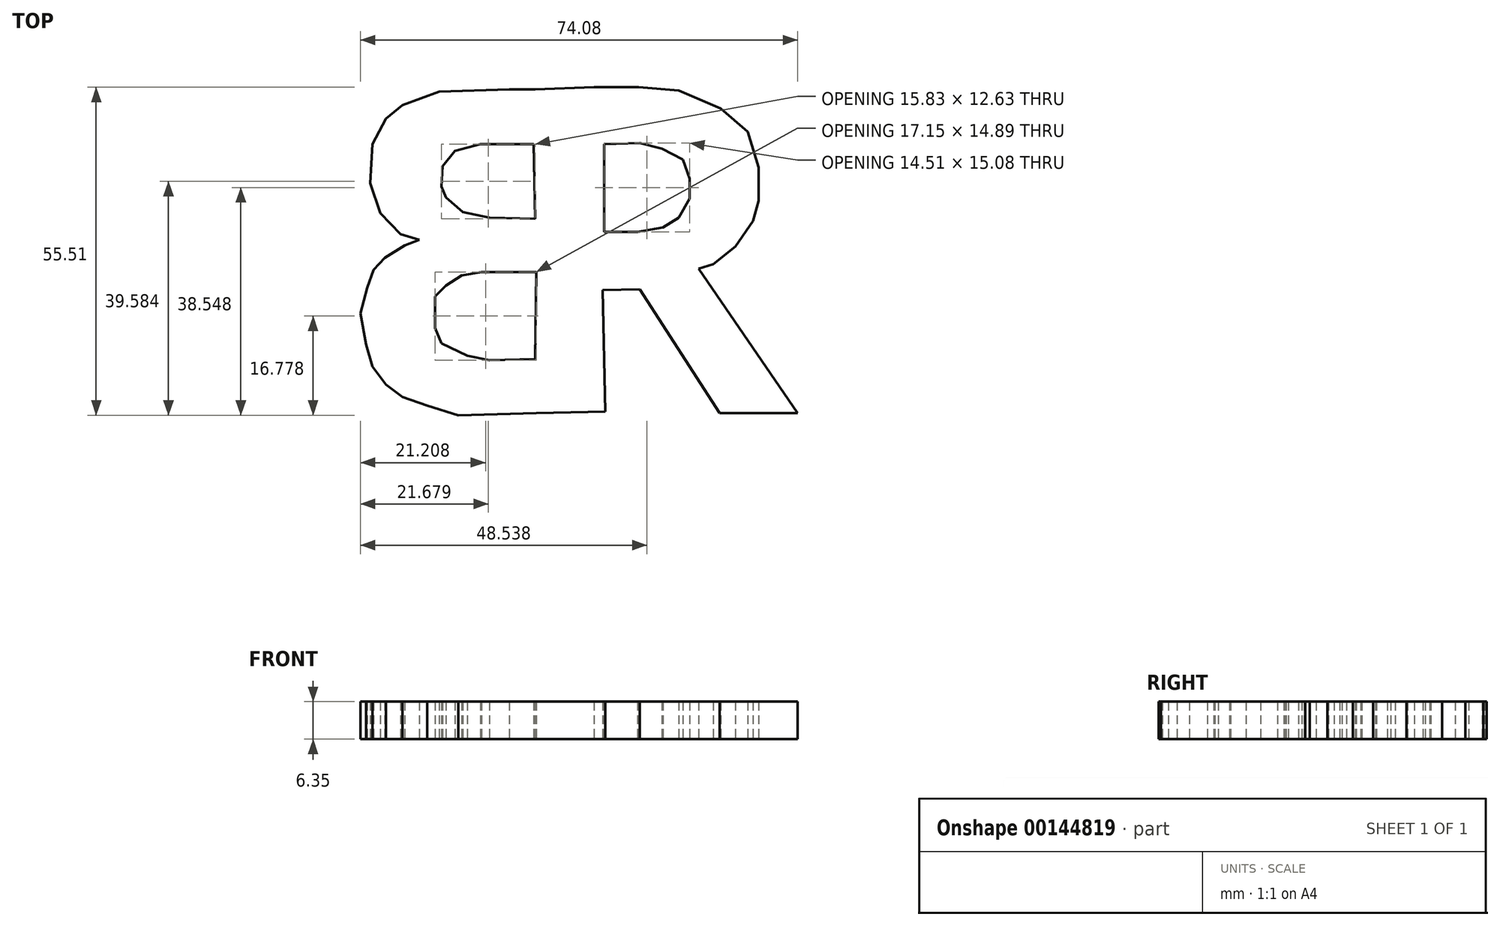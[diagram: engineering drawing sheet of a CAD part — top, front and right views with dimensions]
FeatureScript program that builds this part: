
annotation { "Feature Type Name" : "Feature", "Feature Type Description" : "" }
export const myFeature = defineFeature(function(context is Context, id is Id, definition is map)
    precondition{}
    {
        {
            var Q0;
            Q0=qCreatedBy(makeId("Top.planeOp"),FACE);
            var sketch = newSketch(context, id + "F0", { "sketchPlane" : qUnion([Q0])});
            skLineSegment(sketch, "E0.MirrorCS", {"start": v(-8.3, 21.58) * mm, "end": v(-10.18, 19.7) * mm});
            skLineSegment(sketch, "E1.MirrorCS", {"start": v(0.38, 45.52) * mm, "end": v(-2.45, 45.52) * mm});
            skLineSegment(sketch, "E2.MirrorCS", {"start": v(-9.05, 11.78) * mm, "end": v(-6.6, 10.84) * mm});
            skLineSegment(sketch, "E3.MirrorCS", {"start": v(-8.86, 41.75) * mm, "end": v(-9.05, 38.36) * mm});
            skLineSegment(sketch, "E4.MirrorCS", {"start": v(-8.3, 36.47) * mm, "end": v(-5.47, 34.02) * mm});
            skLineSegment(sketch, "E5.MirrorCS", {"start": v(-2.45, 45.52) * mm, "end": v(-6.79, 44.39) * mm});
            skLineSegment(sketch, "E6.MirrorCS", {"start": v(-15.64, 52.11) * mm, "end": v(-18.47, 49.85) * mm});
            skLineSegment(sketch, "E7.MirrorCS", {"start": v(-4.71, 9.7) * mm, "end": v(-9.05, 11.78) * mm});
            skLineSegment(sketch, "E8.MirrorCS", {"start": v(-15.27, 28.37) * mm, "end": v(-18.66, 26.3) * mm});
            skLineSegment(sketch, "E9.MirrorCS", {"start": v(-18.66, 26.3) * mm, "end": v(-20.54, 24.22) * mm});
            skLineSegment(sketch, "E10.MirrorCS", {"start": v(-12.82, 29.3) * mm, "end": v(-15.27, 28.37) * mm});
            skLineSegment(sketch, "E11.MirrorCS", {"start": v(-15.64, 2.73) * mm, "end": v(-11.5, 1.23) * mm});
            skLineSegment(sketch, "E12.MirrorCS", {"start": v(-10.18, 19.7) * mm, "end": v(-10.18, 17.06) * mm});
            skLineSegment(sketch, "E13.MirrorCS", {"start": v(-10.18, 14.42) * mm, "end": v(-9.05, 11.78) * mm});
            skLineSegment(sketch, "E14.MirrorCS", {"start": v(-10.18, 17.06) * mm, "end": v(-10.18, 14.42) * mm});
            skLineSegment(sketch, "E15.MirrorCS", {"start": v(-16.02, 30.25) * mm, "end": v(-12.82, 29.3) * mm});
            skLineSegment(sketch, "E16.MirrorCS", {"start": v(-19.41, 33.83) * mm, "end": v(-16.02, 30.25) * mm});
            skLineSegment(sketch, "E17.MirrorCS", {"start": v(-4.71, 9.7) * mm, "end": v(-0.94, 8.95) * mm});
            skLineSegment(sketch, "E18.MirrorCS", {"start": v(-6.79, 44.39) * mm, "end": v(-8.86, 41.75) * mm});
            skLineSegment(sketch, "E19.MirrorCS", {"start": v(-18.47, 4.8) * mm, "end": v(-20.73, 7.82) * mm});
            skLineSegment(sketch, "E20.MirrorCS", {"start": v(-18.47, 4.8) * mm, "end": v(-15.64, 2.73) * mm});
            skLineSegment(sketch, "E21.MirrorCS", {"start": v(-20.73, 45.52) * mm, "end": v(-18.47, 49.85) * mm});
            skLineSegment(sketch, "E22.MirrorCS", {"start": v(-5.47, 34.02) * mm, "end": v(-0.94, 33.08) * mm});
            skLineSegment(sketch, "E23.MirrorCS", {"start": v(-9.05, 38.36) * mm, "end": v(-8.3, 36.47) * mm});
            skPoint(sketch, "E24.MirrorP", {"position": v(-10.18, 17.06) * mm});
            skLineSegment(sketch, "E25.MirrorCS", {"start": v(-11.5, 1.23) * mm, "end": v(-6.22, -0.38) * mm});
            skLineSegment(sketch, "E26.MirrorCS", {"start": v(-5.65, 23.28) * mm, "end": v(-8.3, 21.58) * mm});
            skLineSegment(sketch, "E27.MirrorCS", {"start": v(-9.42, 54.38) * mm, "end": v(-15.64, 52.11) * mm});
            skLineSegment(sketch, "E28.MirrorCS", {"start": v(-2.26, 23.84) * mm, "end": v(-5.65, 23.28) * mm});
            skPoint(sketch, "E29.MirrorP", {"position": v(-9.42, 54.38) * mm});
            skPoint(sketch, "E30.MirrorP", {"position": v(-15.64, 2.73) * mm});
            skPoint(sketch, "E31.MirrorP", {"position": v(-18.66, 26.3) * mm});
            skPoint(sketch, "E32.MirrorP", {"position": v(-20.54, 24.22) * mm});
            skPoint(sketch, "E33.MirrorP", {"position": v(-18.47, 4.8) * mm});
            skPoint(sketch, "E34.MirrorP", {"position": v(-0.94, 8.95) * mm});
            skPoint(sketch, "E35.MirrorP", {"position": v(-5.47, 34.02) * mm});
            skPoint(sketch, "E36.MirrorP", {"position": v(-6.6, 10.84) * mm});
            skLineSegment(sketch, "E37.MirrorCS", {"start": v(-0.94, 8.95) * mm, "end": v(6.79, 9.14) * mm});
            skLineSegment(sketch, "E38.MirrorCS", {"start": v(6.97, 23.84) * mm, "end": v(-2.26, 23.84) * mm});
            skPoint(sketch, "E39.MirrorP", {"position": v(-8.3, 21.58) * mm});
            skPoint(sketch, "E40.MirrorP", {"position": v(-2.45, 45.52) * mm});
            skPoint(sketch, "E41.MirrorP", {"position": v(-18.47, 49.85) * mm});
            skPoint(sketch, "E42.MirrorP", {"position": v(-6.22, -0.38) * mm});
            skPoint(sketch, "E43.MirrorP", {"position": v(-0.94, 33.08) * mm});
            skLineSegment(sketch, "E44.MirrorCS", {"start": v(6.57, 45.52) * mm, "end": v(0.38, 45.52) * mm});
            skPoint(sketch, "E45.MirrorP", {"position": v(-15.27, 28.37) * mm});
            skPoint(sketch, "E46.MirrorP", {"position": v(-16.02, 30.25) * mm});
            skPoint(sketch, "E47.MirrorP", {"position": v(0.38, 45.52) * mm});
            skPoint(sketch, "E48.MirrorP", {"position": v(-2.26, 23.84) * mm});
            skPoint(sketch, "E49.MirrorP", {"position": v(-8.86, 41.75) * mm});
            skPoint(sketch, "E50.MirrorP", {"position": v(-5.65, 23.28) * mm});
            skPoint(sketch, "E51.MirrorP", {"position": v(-4.71, 9.7) * mm});
            skPoint(sketch, "E52.MirrorP", {"position": v(-6.79, 44.39) * mm});
            skLineSegment(sketch, "E53.MirrorCS", {"start": v(-19.41, 33.83) * mm, "end": v(-21.1, 38.92) * mm});
            skPoint(sketch, "E54.MirrorP", {"position": v(-19.41, 33.83) * mm});
            skLineSegment(sketch, "E55.MirrorCS", {"start": v(-20.73, 45.52) * mm, "end": v(-21.1, 38.92) * mm});
            skPoint(sketch, "E56.MirrorP", {"position": v(-11.5, 1.23) * mm});
            skPoint(sketch, "E57.MirrorP", {"position": v(-15.64, 52.11) * mm});
            skPoint(sketch, "E58.MirrorP", {"position": v(-12.82, 29.3) * mm});
            skPoint(sketch, "E59.MirrorP", {"position": v(-10.18, 19.7) * mm});
            skPoint(sketch, "E60.MirrorP", {"position": v(-9.05, 11.78) * mm});
            skPoint(sketch, "E61.MirrorP", {"position": v(-8.3, 36.47) * mm});
            skPoint(sketch, "E62.MirrorP", {"position": v(-22.8, 16.87) * mm});
            skPoint(sketch, "E63.MirrorP", {"position": v(-9.05, 38.36) * mm});
            skPoint(sketch, "E64.MirrorP", {"position": v(-10.18, 14.42) * mm});
            skLineSegment(sketch, "E65.MirrorCS", {"start": v(-21.68, 21.2) * mm, "end": v(-22.8, 16.87) * mm});
            skLineSegment(sketch, "E66.MirrorCS", {"start": v(-20.54, 24.22) * mm, "end": v(-21.68, 21.2) * mm});
            skLineSegment(sketch, "E67.MirrorCS", {"start": v(-18.47, 49.85) * mm, "end": v(-20.73, 45.52) * mm});
            skLineSegment(sketch, "E68.MirrorCS", {"start": v(-20.73, 7.82) * mm, "end": v(-18.47, 4.8) * mm});
            skLineSegment(sketch, "E69.MirrorCS", {"start": v(-4.71, 9.7) * mm, "end": v(-6.6, 10.84) * mm});
            skLineSegment(sketch, "E70.MirrorCS", {"start": v(-21.1, 38.92) * mm, "end": v(-19.41, 33.83) * mm});
            skLineSegment(sketch, "E71.MirrorCS", {"start": v(-22.8, 16.87) * mm, "end": v(-21.86, 11.6) * mm});
            skPoint(sketch, "E72.MirrorP", {"position": v(3.01, 45.44) * mm});
            skPoint(sketch, "E73.MirrorP", {"position": v(2.45, 54.76) * mm});
            skLineSegment(sketch, "E74.MirrorCS", {"start": v(2.45, 54.76) * mm, "end": v(-9.42, 54.38) * mm});
            skPoint(sketch, "E75.MirrorP", {"position": v(-20.73, 7.82) * mm});
            skPoint(sketch, "E76.MirrorP", {"position": v(-20.73, 45.52) * mm});
            skPoint(sketch, "E77.MirrorP", {"position": v(6.79, 32.89) * mm});
            skPoint(sketch, "E78.MirrorP", {"position": v(6.97, 23.84) * mm});
            skPoint(sketch, "E79.MirrorP", {"position": v(-21.86, 11.6) * mm});
            skLineSegment(sketch, "E80.MirrorCS", {"start": v(3.01, 45.44) * mm, "end": v(0.38, 45.52) * mm});
            skPoint(sketch, "E81.MirrorP", {"position": v(-21.68, 21.2) * mm});
            skPoint(sketch, "E82.MirrorP", {"position": v(6.79, 9.14) * mm});
            skLineSegment(sketch, "E83.MirrorCS", {"start": v(-0.94, 33.08) * mm, "end": v(6.79, 32.89) * mm});
            skPoint(sketch, "E84.MirrorP", {"position": v(-21.1, 38.92) * mm});
            skPoint(sketch, "E85", {"position": v(6.79, 54.76) * mm});
            skPoint(sketch, "E86", {"position": v(6.97, 0) * mm});
            skLineSegment(sketch, "E87", {"start": v(2.45, 54.76) * mm, "end": v(6.79, 54.76) * mm});
            skLineSegment(sketch, "E88", {"start": v(6.79, 54.76) * mm, "end": v(6.57, 45.52) * mm});
            skLineSegment(sketch, "E89", {"start": v(6.79, 32.89) * mm, "end": v(6.97, 23.84) * mm});
            skLineSegment(sketch, "E90", {"start": v(6.79, 9.14) * mm, "end": v(6.97, 0) * mm});
            skLineSegment(sketch, "E91", {"start": v(6.97, 0) * mm, "end": v(-6.22, -0.38) * mm});
            skLineSegment(sketch, "E92", {"start": v(-20.73, 7.82) * mm, "end": v(-21.86, 11.6) * mm});
            skLineSegment(sketch, "E93", {"start": v(6.97, 0) * mm, "end": v(18.66, 0.24) * mm});
            skLineSegment(sketch, "E94", {"start": v(18.66, 0.24) * mm, "end": v(18.23, 20.81) * mm});
            skLineSegment(sketch, "E95", {"start": v(18.23, 20.81) * mm, "end": v(24.5, 20.94) * mm});
            skLineSegment(sketch, "E96", {"start": v(24.5, 20.94) * mm, "end": v(38.07, 0) * mm});
            skLineSegment(sketch, "E97", {"start": v(38.07, 0) * mm, "end": v(51.27, 0) * mm});
            skLineSegment(sketch, "E98", {"start": v(51.27, 0) * mm, "end": v(34.5, 24.4) * mm});
            skPoint(sketch, "E99", {"position": v(36.94, 25.16) * mm});
            skPoint(sketch, "E100", {"position": v(40.71, 28.18) * mm});
            skPoint(sketch, "E101", {"position": v(43.73, 32.51) * mm});
            skPoint(sketch, "E102", {"position": v(44.67, 35.9) * mm});
            skPoint(sketch, "E103", {"position": v(44.67, 41.56) * mm});
            skPoint(sketch, "E104", {"position": v(42.79, 47.6) * mm});
            skPoint(sketch, "E105", {"position": v(38.26, 51.55) * mm});
            skPoint(sketch, "E106", {"position": v(31.1, 54.57) * mm});
            skPoint(sketch, "E107", {"position": v(24.31, 55.13) * mm});
            skPoint(sketch, "E108", {"position": v(16.77, 55.13) * mm});
            skLineSegment(sketch, "E109", {"start": v(6.79, 54.76) * mm, "end": v(16.77, 55.13) * mm});
            skLineSegment(sketch, "E110", {"start": v(16.77, 55.13) * mm, "end": v(24.31, 55.13) * mm});
            skLineSegment(sketch, "E111", {"start": v(24.31, 55.13) * mm, "end": v(31.1, 54.57) * mm});
            skLineSegment(sketch, "E112", {"start": v(31.1, 54.57) * mm, "end": v(38.26, 51.55) * mm});
            skLineSegment(sketch, "E113", {"start": v(38.26, 51.55) * mm, "end": v(42.79, 47.6) * mm});
            skLineSegment(sketch, "E114", {"start": v(42.79, 47.6) * mm, "end": v(44.67, 41.56) * mm});
            skLineSegment(sketch, "E115", {"start": v(44.67, 41.56) * mm, "end": v(44.67, 35.9) * mm});
            skLineSegment(sketch, "E116", {"start": v(44.67, 35.9) * mm, "end": v(43.73, 32.51) * mm});
            skLineSegment(sketch, "E117", {"start": v(43.73, 32.51) * mm, "end": v(40.71, 28.18) * mm});
            skLineSegment(sketch, "E118", {"start": v(40.71, 28.18) * mm, "end": v(36.94, 25.16) * mm});
            skLineSegment(sketch, "E119", {"start": v(36.94, 25.16) * mm, "end": v(34.5, 24.4) * mm});
            skLineSegment(sketch, "E120", {"start": v(18.47, 45.52) * mm, "end": v(18.47, 30.63) * mm});
            skPoint(sketch, "E121", {"position": v(24.13, 30.63) * mm});
            skPoint(sketch, "E122", {"position": v(28.46, 31.38) * mm});
            skPoint(sketch, "E123", {"position": v(31.1, 33.08) * mm});
            skPoint(sketch, "E124", {"position": v(32.98, 36.28) * mm});
            skPoint(sketch, "E125", {"position": v(32.98, 39.68) * mm});
            skPoint(sketch, "E126", {"position": v(31.85, 42.88) * mm});
            skPoint(sketch, "E127", {"position": v(28.27, 44.77) * mm});
            skPoint(sketch, "E128", {"position": v(24.5, 45.7) * mm});
            skLineSegment(sketch, "E129", {"start": v(18.47, 45.52) * mm, "end": v(24.5, 45.7) * mm});
            skLineSegment(sketch, "E130", {"start": v(24.5, 45.7) * mm, "end": v(28.27, 44.77) * mm});
            skLineSegment(sketch, "E131", {"start": v(28.27, 44.77) * mm, "end": v(31.85, 42.88) * mm});
            skLineSegment(sketch, "E132", {"start": v(31.85, 42.88) * mm, "end": v(32.98, 39.68) * mm});
            skLineSegment(sketch, "E133", {"start": v(32.98, 39.68) * mm, "end": v(32.98, 36.28) * mm});
            skLineSegment(sketch, "E134", {"start": v(32.98, 36.28) * mm, "end": v(31.1, 33.08) * mm});
            skLineSegment(sketch, "E135", {"start": v(31.1, 33.08) * mm, "end": v(28.46, 31.38) * mm});
            skLineSegment(sketch, "E136", {"start": v(28.46, 31.38) * mm, "end": v(24.13, 30.63) * mm});
            skLineSegment(sketch, "E137", {"start": v(24.13, 30.63) * mm, "end": v(18.47, 30.63) * mm});
            skLineSegment(sketch, "E138", {"start": v(6.57, 45.52) * mm, "end": v(6.79, 32.89) * mm});
            skLineSegment(sketch, "E139", {"start": v(6.97, 23.84) * mm, "end": v(6.79, 9.14) * mm});
            skSolve(sketch);
        }
        {
            var Q0;
            Q0=makeQuery(id+"F0.imprint","IMPRINT",FACE,{"disambiguationData":[TD([[makeQuery(id+"F0.imprint","IMPRINT",EDGE,{"derivedFrom":sQuery(id+"F0.wireOp",EDGE,"E88")}),1.0]])]});
            extrude(context, id + "F1", {"entities" : qUnion([Q0]), "depth" : 6.35 * mm});
        }
        {
            var Q0;
            Q0=makeQuery(id+"F0.imprint","IMPRINT",FACE,{"disambiguationData":[TD([[makeQuery(id+"F0.imprint","IMPRINT",EDGE,{"derivedFrom":sQuery(id+"F0.wireOp",EDGE,"E7.MirrorCS")}),1.0]])]});
            extrude(context, id + "F2", {"entities" : qUnion([Q0]), "operationType" : NewBodyOperationType.ADD, "depth" : 6.35 * mm});
        }
    });
